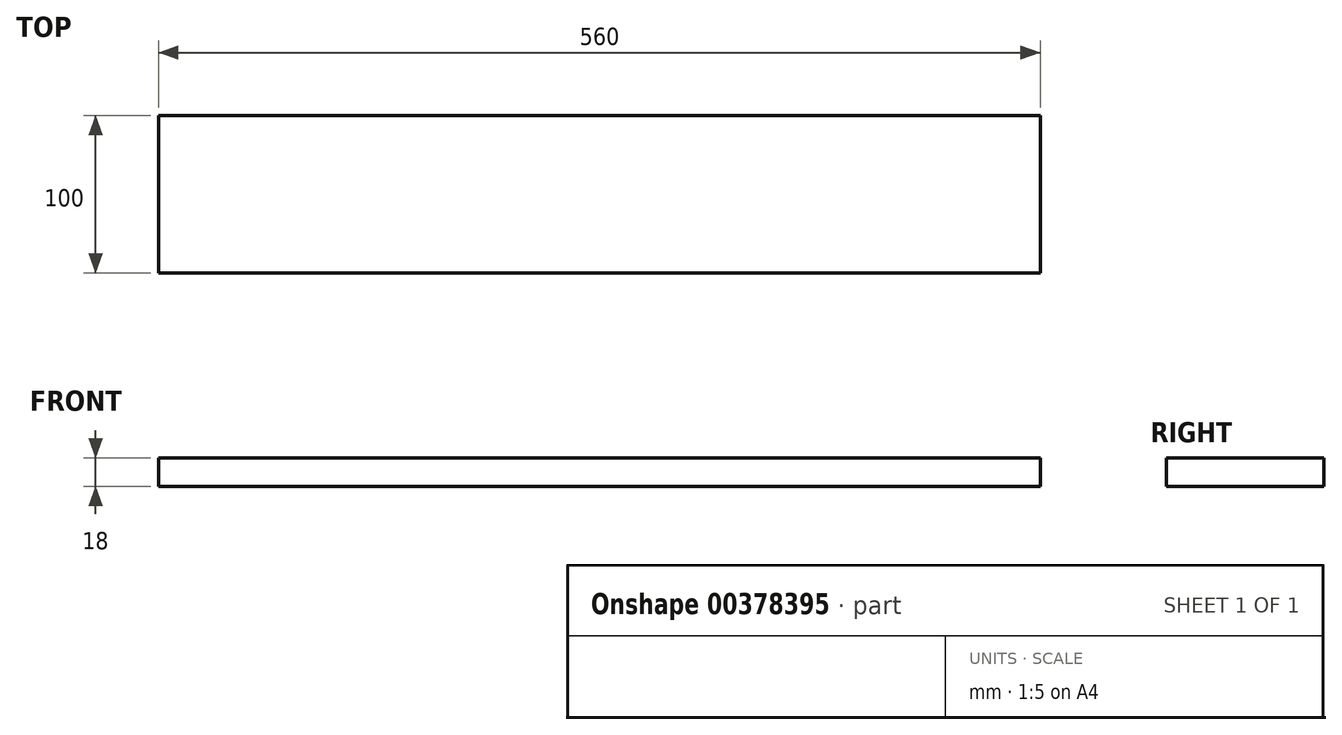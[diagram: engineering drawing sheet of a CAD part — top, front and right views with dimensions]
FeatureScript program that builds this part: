
annotation { "Feature Type Name" : "Feature", "Feature Type Description" : "" }
export const myFeature = defineFeature(function(context is Context, id is Id, definition is map)
    precondition{}
    {
        {
            var Q0;
            Q0=qCreatedBy(makeId("Right.planeOp"),FACE);
            var sketch = newSketch(context, id + "F0", { "sketchPlane" : qUnion([Q0])});
            skLineSegment(sketch, "E0.bottom", {"start": v(50, -9) * mm, "end": v(-50, -9) * mm});
            skLineSegment(sketch, "E0.top", {"start": v(50, 9) * mm, "end": v(-50, 9) * mm});
            skLineSegment(sketch, "E0.left", {"start": v(50, -9) * mm, "end": v(50, 9) * mm});
            skLineSegment(sketch, "E0.right", {"start": v(-50, -9) * mm, "end": v(-50, 9) * mm});
            skPoint(sketch, "E0.middle", {"position": v(0, 0) * mm});
            skSolve(sketch);
        }
        {
            var Q0;
            Q0=qSketchRegion(id+"F0",true);
            extrude(context, id + "F1", {"entities" : qUnion([Q0]), "depth" : 560 * mm});
        }
    });
